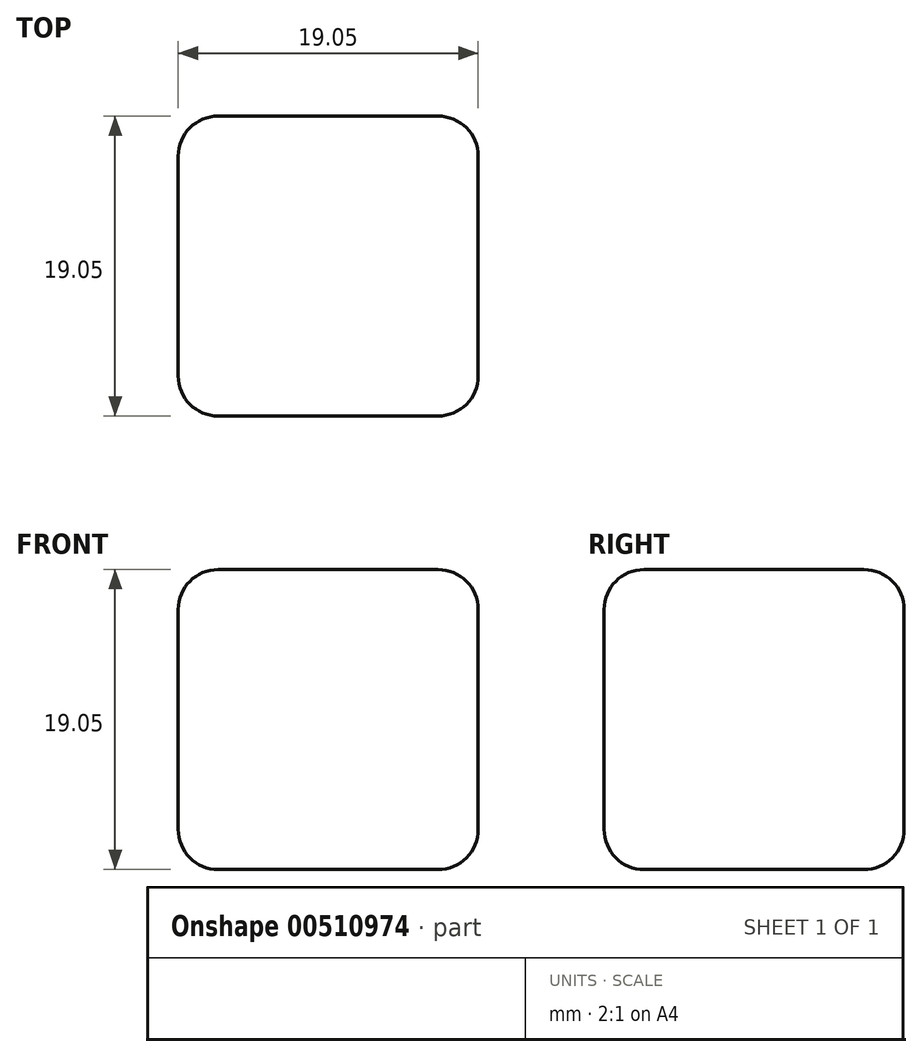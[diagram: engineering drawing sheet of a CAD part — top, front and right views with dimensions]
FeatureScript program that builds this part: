
annotation { "Feature Type Name" : "Feature", "Feature Type Description" : "" }
export const myFeature = defineFeature(function(context is Context, id is Id, definition is map)
    precondition{}
    {
        {
            var Q0;
            Q0=qCreatedBy(makeId("Front.planeOp"),FACE);
            var sketch = newSketch(context, id + "F0", { "sketchPlane" : qUnion([Q0])});
            skLineSegment(sketch, "E0.bottom", {"start": v(-14.01, 12.77) * mm, "end": v(5.04, 12.77) * mm});
            skLineSegment(sketch, "E0.top", {"start": v(-14.01, -6.28) * mm, "end": v(5.04, -6.28) * mm});
            skLineSegment(sketch, "E0.left", {"start": v(-14.01, 12.77) * mm, "end": v(-14.01, -6.28) * mm});
            skLineSegment(sketch, "E0.right", {"start": v(5.04, 12.77) * mm, "end": v(5.04, -6.28) * mm});
            skSolve(sketch);
        }
        {
            var Q0;
            Q0 = qSketchRegion(id + "F0", true);
            extrude(context, id + "F1", {"entities" : qUnion([Q0]), "depth" : 19.05 * mm});
        }
        {
            var Q0;
            Q0=makeQuery(id+"F1.opExtrude","CAP_EDGE",EDGE,{"disambiguationData":[OSD([sQuery(id+"F0.wireOp",EDGE,"E0.bottom")])],"isStart":false});
            var Q1;
            Q1=makeQuery(id+"F1.opExtrude","SWEPT_EDGE",EDGE,{"disambiguationData":[OSD([sQuery(id+"F0.wireOp",EDGE,"E0.bottom"),sQuery(id+"F0.wireOp",EDGE,"E0.right")])]});
            var Q2;
            Q2=makeQuery(id+"F1.opExtrude","CAP_EDGE",EDGE,{"disambiguationData":[OSD([sQuery(id+"F0.wireOp",EDGE,"E0.right")])],"isStart":false});
            var Q3;
            Q3=makeQuery(id+"F1.opExtrude","CAP_EDGE",EDGE,{"disambiguationData":[OSD([sQuery(id+"F0.wireOp",EDGE,"E0.right")])],"isStart":true});
            var Q4;
            Q4=makeQuery(id+"F1.opExtrude","CAP_EDGE",EDGE,{"disambiguationData":[OSD([sQuery(id+"F0.wireOp",EDGE,"E0.bottom")])],"isStart":true});
            var Q5;
            Q5=makeQuery(id+"F1.opExtrude","SWEPT_EDGE",EDGE,{"disambiguationData":[OSD([sQuery(id+"F0.wireOp",EDGE,"E0.bottom"),sQuery(id+"F0.wireOp",EDGE,"E0.left")])]});
            var Q6;
            Q6=makeQuery(id+"F1.opExtrude","CAP_EDGE",EDGE,{"disambiguationData":[OSD([sQuery(id+"F0.wireOp",EDGE,"E0.left")])],"isStart":true});
            var Q7;
            Q7=makeQuery(id+"F1.opExtrude","CAP_EDGE",EDGE,{"disambiguationData":[OSD([sQuery(id+"F0.wireOp",EDGE,"E0.top")])],"isStart":true});
            var Q8;
            Q8=makeQuery(id+"F1.opExtrude","SWEPT_EDGE",EDGE,{"disambiguationData":[OSD([sQuery(id+"F0.wireOp",EDGE,"E0.top"),sQuery(id+"F0.wireOp",EDGE,"E0.left")])]});
            var Q9;
            Q9=makeQuery(id+"F1.opExtrude","CAP_EDGE",EDGE,{"disambiguationData":[OSD([sQuery(id+"F0.wireOp",EDGE,"E0.top")])],"isStart":false});
            var Q10;
            Q10=makeQuery(id+"F1.opExtrude","CAP_EDGE",EDGE,{"disambiguationData":[OSD([sQuery(id+"F0.wireOp",EDGE,"E0.left")])],"isStart":false});
            var Q11;
            Q11=makeQuery(id+"F1.opExtrude","SWEPT_EDGE",EDGE,{"disambiguationData":[OSD([sQuery(id+"F0.wireOp",EDGE,"E0.top"),sQuery(id+"F0.wireOp",EDGE,"E0.right")])]});
            fillet(context, id + "F2", {"entities" : qUnion([Q0, Q1, Q2, Q3, Q4, Q5, Q6, Q7, Q8, Q9, Q10, Q11]), "radius" : 2.54 * mm, "tangentPropagation" : true, "allowEdgeOverflow" : false});
        }
    });
